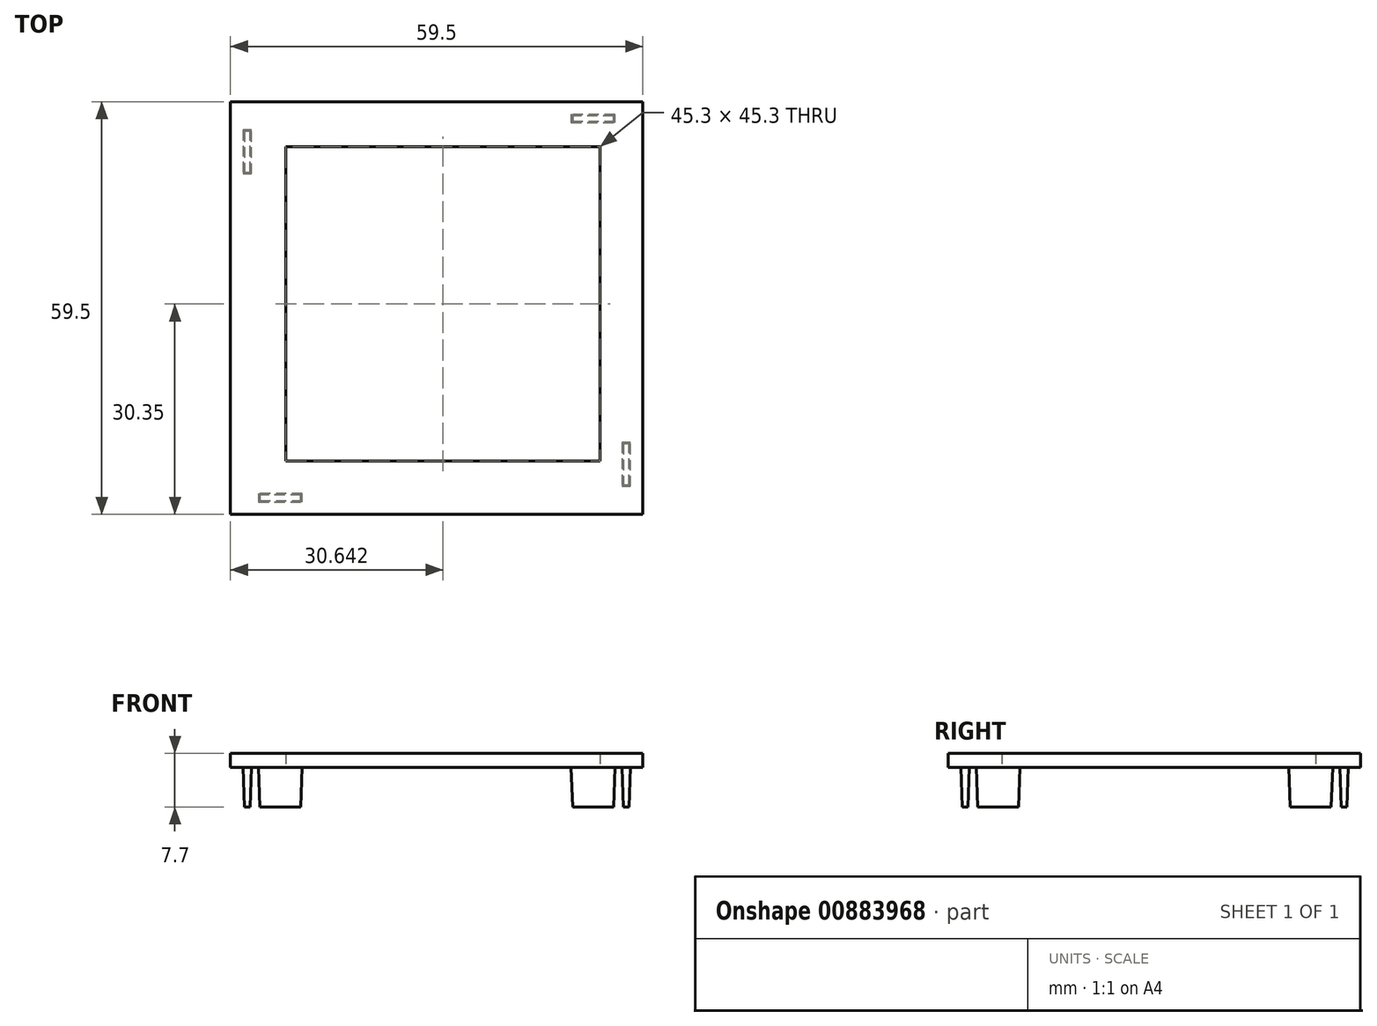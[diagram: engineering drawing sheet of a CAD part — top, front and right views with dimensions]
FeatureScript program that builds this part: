
annotation { "Feature Type Name" : "Feature", "Feature Type Description" : "" }
export const myFeature = defineFeature(function(context is Context, id is Id, definition is map)
    precondition{}
    {
        {
            var Q0;
            Q0=qCreatedBy(makeId("Top.planeOp"),FACE);
            var sketch = newSketch(context, id + "F0", { "sketchPlane" : qUnion([Q0])});
            skLineSegment(sketch, "E0.bottom", {"start": v(29.75, -29.75) * mm, "end": v(-29.75, -29.75) * mm});
            skLineSegment(sketch, "E0.top", {"start": v(29.75, 29.75) * mm, "end": v(-29.75, 29.75) * mm});
            skLineSegment(sketch, "E0.left", {"start": v(29.75, -29.75) * mm, "end": v(29.75, 29.75) * mm});
            skLineSegment(sketch, "E0.right", {"start": v(-29.75, -29.75) * mm, "end": v(-29.75, 29.75) * mm});
            skPoint(sketch, "E0.middle", {"position": v(0, 0) * mm});
            skLineSegment(sketch, "E1.bottom", {"start": v(-21.76, -22.05) * mm, "end": v(23.54, -22.05) * mm});
            skLineSegment(sketch, "E1.top", {"start": v(-21.76, 23.25) * mm, "end": v(23.54, 23.25) * mm});
            skLineSegment(sketch, "E1.left", {"start": v(-21.76, -22.05) * mm, "end": v(-21.76, 23.25) * mm});
            skLineSegment(sketch, "E1.right", {"start": v(23.54, -22.05) * mm, "end": v(23.54, 23.25) * mm});
            skSolve(sketch);
        }
        {
            var Q0;
            Q0=makeQuery(id+"F0.imprint","IMPRINT",FACE,{"disambiguationData":[TD([[makeQuery(id+"F0.imprint","IMPRINT",EDGE,{"derivedFrom":sQuery(id+"F0.wireOp",EDGE,"E0.bottom")}),-1.0]])]});
            extrude(context, id + "F1", {"entities" : qUnion([Q0]), "depth" : 2 * mm, "offsetDistance" : 25 * mm});
        }
        {
            var Q0;
            Q0=makeQuery(id+"F1.opExtrude","CAP_FACE",FACE,{"disambiguationData":[OSD([sQuery(id+"F0.wireOp",EDGE,"E0.bottom"),sQuery(id+"F0.wireOp",EDGE,"E0.top"),sQuery(id+"F0.wireOp",EDGE,"E0.left"),sQuery(id+"F0.wireOp",EDGE,"E0.right"),sQuery(id+"F0.wireOp",EDGE,"E1.bottom"),sQuery(id+"F0.wireOp",EDGE,"E1.top"),sQuery(id+"F0.wireOp",EDGE,"E1.left"),sQuery(id+"F0.wireOp",EDGE,"E1.right")])],"isStart":true});
            var sketch = newSketch(context, id + "F2", { "sketchPlane" : qUnion([Q0])});
            skPoint(sketch, "E2.startSnap0", {"position": v(23.54, -0.6) * mm});
            skLineSegment(sketch, "E3.bottom", {"start": v(23.54, 18.55) * mm, "end": v(24.74, 18.55) * mm});
            skLineSegment(sketch, "E3.top", {"start": v(23.54, -19.75) * mm, "end": v(24.74, -19.75) * mm});
            skLineSegment(sketch, "E3.left", {"start": v(23.54, 18.55) * mm, "end": v(23.54, -19.75) * mm});
            skLineSegment(sketch, "E3.right", {"start": v(24.74, 18.55) * mm, "end": v(24.74, -19.75) * mm});
            skLineSegment(sketch, "E4", {"start": v(24.74, -19.25) * mm, "end": v(29.24, -19.25) * mm, "construction": true});
            skLineSegment(sketch, "E5", {"start": v(26.47, -19.25) * mm, "end": v(26.47, -17.68) * mm, "construction": true});
            skCircle(sketch, "E6", {"center": v(26.47, -17.68) * mm, "radius": 1.57 * mm});
            skLineSegment(sketch, "E7.bottom", {"start": v(26.74, 19.4) * mm, "end": v(27.94, 19.4) * mm});
            skLineSegment(sketch, "E7.top", {"start": v(26.74, 25.7) * mm, "end": v(27.94, 25.7) * mm});
            skLineSegment(sketch, "E7.left", {"start": v(26.74, 19.4) * mm, "end": v(26.74, 25.7) * mm});
            skLineSegment(sketch, "E7.right", {"start": v(27.94, 19.4) * mm, "end": v(27.94, 25.7) * mm});
            skLineSegment(sketch, "E8.1.0", {"start": v(19.4, -26.74) * mm, "end": v(25.7, -26.74) * mm});
            skLineSegment(sketch, "E8.1.1", {"start": v(19.4, -27.94) * mm, "end": v(25.7, -27.94) * mm});
            skLineSegment(sketch, "E8.1.2", {"start": v(25.7, -26.74) * mm, "end": v(25.7, -27.94) * mm});
            skLineSegment(sketch, "E8.1.3", {"start": v(19.4, -26.74) * mm, "end": v(19.4, -27.94) * mm});
            skLineSegment(sketch, "E8.2.0", {"start": v(-26.74, -19.4) * mm, "end": v(-26.74, -25.7) * mm});
            skLineSegment(sketch, "E8.2.1", {"start": v(-27.94, -19.4) * mm, "end": v(-27.94, -25.7) * mm});
            skLineSegment(sketch, "E8.2.2", {"start": v(-26.74, -25.7) * mm, "end": v(-27.94, -25.7) * mm});
            skLineSegment(sketch, "E8.2.3", {"start": v(-26.74, -19.4) * mm, "end": v(-27.94, -19.4) * mm});
            skLineSegment(sketch, "E8.3.0", {"start": v(-19.4, 26.74) * mm, "end": v(-25.7, 26.74) * mm});
            skLineSegment(sketch, "E8.3.1", {"start": v(-19.4, 27.94) * mm, "end": v(-25.7, 27.94) * mm});
            skLineSegment(sketch, "E8.3.2", {"start": v(-25.7, 26.74) * mm, "end": v(-25.7, 27.94) * mm});
            skLineSegment(sketch, "E8.3.3", {"start": v(-19.4, 26.74) * mm, "end": v(-19.4, 27.94) * mm});
            skPoint(sketch, "E8.center", {"position": v(0, 0) * mm});
            skLineSegment(sketch, "E8.anchor1", {"start": v(0, 0) * mm, "end": v(26.74, 19.4) * mm, "construction": true});
            skLineSegment(sketch, "E8.anchor2", {"start": v(0, 0) * mm, "end": v(-19.4, 26.74) * mm, "construction": true});
            skSolve(sketch);
        }
        {
            var Q0;
            Q0=makeQuery(id+"F2.imprint","IMPRINT",FACE,{"disambiguationData":[TD([[makeQuery(id+"F2.imprint","IMPRINT",EDGE,{"derivedFrom":sQuery(id+"F2.wireOp",EDGE,"E7.bottom")}),1.0]])]});
            var Q1;
            Q1=makeQuery(id+"F2.imprint","IMPRINT",FACE,{"disambiguationData":[TD([[makeQuery(id+"F2.imprint","IMPRINT",EDGE,{"derivedFrom":sQuery(id+"F2.wireOp",EDGE,"d2ffc4b8-9039-4fde-a5e4-fea8735ca343.1.6")}),-1.0]])]});
            var Q2;
            Q2=makeQuery(id+"F2.imprint","IMPRINT",FACE,{"disambiguationData":[TD([[makeQuery(id+"F2.imprint","IMPRINT",EDGE,{"derivedFrom":sQuery(id+"F2.wireOp",EDGE,"d2ffc4b8-9039-4fde-a5e4-fea8735ca343.2.6")}),-1.0]])]});
            var Q3;
            Q3=makeQuery(id+"F2.imprint","IMPRINT",FACE,{"disambiguationData":[TD([[makeQuery(id+"F2.imprint","IMPRINT",EDGE,{"derivedFrom":sQuery(id+"F2.wireOp",EDGE,"d2ffc4b8-9039-4fde-a5e4-fea8735ca343.3.6")}),-1.0]])]});
            var Q4;
            Q4=makeQuery(id+"F2.imprint","IMPRINT",FACE,{"disambiguationData":[TD([[makeQuery(id+"F2.imprint","IMPRINT",EDGE,{"derivedFrom":sQuery(id+"F2.wireOp",EDGE,"E8.1.0")}),-1.0]])]});
            var Q5;
            Q5=makeQuery(id+"F2.imprint","IMPRINT",FACE,{"disambiguationData":[TD([[makeQuery(id+"F2.imprint","IMPRINT",EDGE,{"derivedFrom":sQuery(id+"F2.wireOp",EDGE,"E8.2.0")}),-1.0]])]});
            var Q6;
            Q6=makeQuery(id+"F2.imprint","IMPRINT",FACE,{"disambiguationData":[TD([[makeQuery(id+"F2.imprint","IMPRINT",EDGE,{"derivedFrom":sQuery(id+"F2.wireOp",EDGE,"E8.3.0")}),-1.0]])]});
            extrude(context, id + "F3", {"entities" : qUnion([Q0, Q1, Q2, Q3, Q4, Q5, Q6]), "operationType" : NewBodyOperationType.ADD, "depth" : 5.7 * mm, "offsetDistance" : 25 * mm, "hasDraft" : true, "draftAngle" : 2 * degree, "draftPullDirection" : true});
        }
    });
